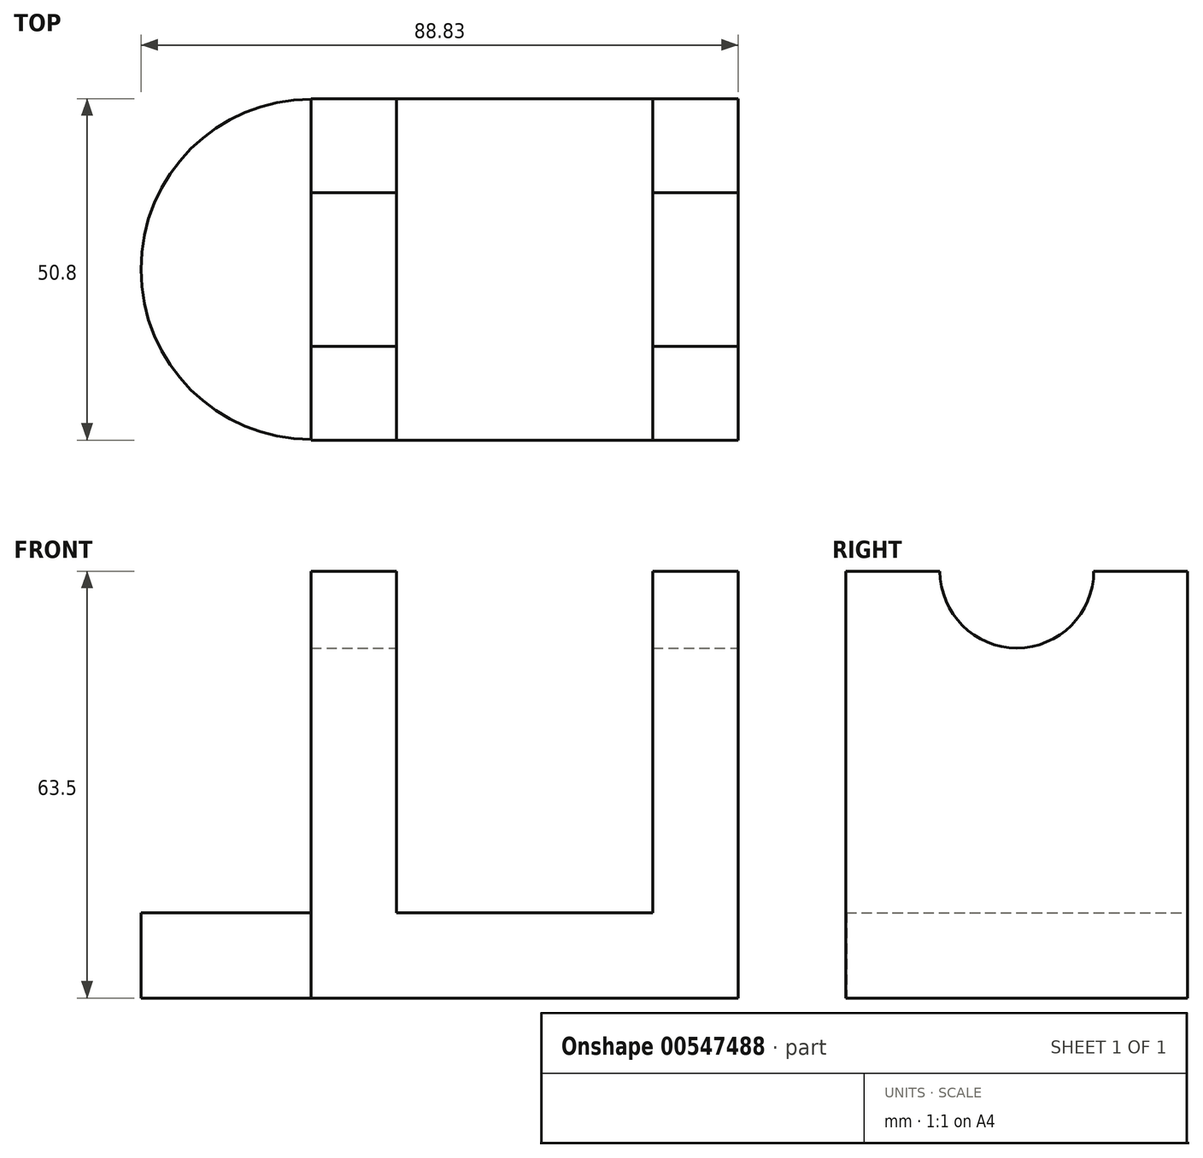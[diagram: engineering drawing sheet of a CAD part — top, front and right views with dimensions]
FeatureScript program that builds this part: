
annotation { "Feature Type Name" : "Feature", "Feature Type Description" : "" }
export const myFeature = defineFeature(function(context is Context, id is Id, definition is map)
    precondition{}
    {
        {
            var Q0;
            Q0=qCreatedBy(makeId("Front.planeOp"),FACE);
            var sketch = newSketch(context, id + "F0", { "sketchPlane" : qUnion([Q0])});
            skLineSegment(sketch, "E0", {"start": v(0, 0) * mm, "end": v(-31.75, 0) * mm});
            skLineSegment(sketch, "E1", {"start": v(-31.75, 0) * mm, "end": v(-31.75, 63.5) * mm});
            skLineSegment(sketch, "E2.MirrorCS", {"start": v(31.75, 0) * mm, "end": v(31.75, 63.5) * mm});
            skLineSegment(sketch, "E3.MirrorCS", {"start": v(0, 0) * mm, "end": v(31.75, 0) * mm});
            skLineSegment(sketch, "E4.0", {"start": v(-19.05, 12.7) * mm, "end": v(-19.05, 63.5) * mm});
            skLineSegment(sketch, "E4.1", {"start": v(0, 12.7) * mm, "end": v(-19.05, 12.7) * mm});
            skLineSegment(sketch, "E4.2", {"start": v(0, 12.7) * mm, "end": v(19.05, 12.7) * mm});
            skLineSegment(sketch, "E4.3", {"start": v(19.05, 12.7) * mm, "end": v(19.05, 63.5) * mm});
            skLineSegment(sketch, "E5", {"start": v(-31.75, 63.5) * mm, "end": v(-19.05, 63.5) * mm});
            skLineSegment(sketch, "E6", {"start": v(19.05, 63.5) * mm, "end": v(31.75, 63.5) * mm});
            skSolve(sketch);
        }
        {
            var Q0;
            Q0=makeQuery(id+"F0.imprint","IMPRINT",FACE,{"disambiguationData":[TD([[makeQuery(id+"F0.imprint","IMPRINT",EDGE,{"derivedFrom":sQuery(id+"F0.wireOp",EDGE,"E0")}),-1.0]])]});
            extrude(context, id + "F1", {"entities" : qUnion([Q0]), "endBound" : BoundingType.SYMMETRIC, "depth" : 50.8 * mm, "offsetDistance" : 25.4 * mm});
        }
        {
            var Q0;
            Q0=makeQuery(id+"F1.opExtrude","SWEPT_FACE",FACE,{"disambiguationData":[OSD([sQuery(id+"F0.wireOp",EDGE,"E2.MirrorCS")])]});
            var sketch = newSketch(context, id + "F2", { "sketchPlane" : qUnion([Q0])});
            skCircle(sketch, "E7", {"center": v(0, 63.5) * mm, "radius": 11.43 * mm});
            skSolve(sketch);
        }
        {
            var Q0;
            {var subQ0=sQuery(id+"F2.wireOp",EDGE,"E7");var subQ1=makeQuery(id+"F1.opExtrude","SWEPT_EDGE",EDGE,{"disambiguationData":[OSD([sQuery(id+"F0.wireOp",EDGE,"E2.MirrorCS"),sQuery(id+"F0.wireOp",EDGE,"E6")])]});var subQ2=makeQuery(id+"F2.imprint","INTERSECT",VERTEX,{"disambiguationData":[OD(0.0)],"derivedFrom":[subQ1,subQ0]});Q0=makeQuery(id+"F2.imprint","IMPRINT",FACE,{"disambiguationData":[TD([[makeQuery(id+"F2.imprint","IMPRINT",EDGE,{"disambiguationData":[TD([[subQ2,1.0]])],"derivedFrom":subQ0}),1.0]])]});}
            extrude(context, id + "F3", {"entities" : qUnion([Q0]), "operationType" : NewBodyOperationType.REMOVE, "endBound" : BoundingType.THROUGH_ALL, "oppositeDirection" : true, "depth" : 25.4 * mm, "offsetDistance" : 25.4 * mm});
        }
        {
            var Q0;
            Q0=makeQuery(id+"F1.opExtrude","SWEPT_FACE",FACE,{"disambiguationData":[OSD([sQuery(id+"F0.wireOp",EDGE,"E0"),sQuery(id+"F0.wireOp",EDGE,"E3.MirrorCS")])]});
            var sketch = newSketch(context, id + "F4", { "sketchPlane" : qUnion([Q0])});
            skCircle(sketch, "E8", {"center": v(-31.75, 0) * mm, "radius": 25.33 * mm});
            skCircle(sketch, "E9.MirrorC", {"center": v(31.75, 0) * mm, "radius": 25.33 * mm});
            skSolve(sketch);
        }
        {
            var Q0;
            {var subQ0=sQuery(id+"F4.wireOp",EDGE,"E8");var subQ1=makeQuery(id+"F1.opExtrude","SWEPT_EDGE",EDGE,{"disambiguationData":[OSD([sQuery(id+"F0.wireOp",EDGE,"E0"),sQuery(id+"F0.wireOp",EDGE,"E1")])]});var subQ2=makeQuery(id+"F4.imprint","INTERSECT",VERTEX,{"disambiguationData":[OD(0.0)],"derivedFrom":[subQ1,subQ0]});Q0=makeQuery(id+"F4.imprint","IMPRINT",FACE,{"disambiguationData":[TD([[makeQuery(id+"F4.imprint","IMPRINT",EDGE,{"disambiguationData":[TD([[subQ2,1.0]])],"derivedFrom":subQ0}),1.0]])]});}
            var Q1;
            {var subQ0=sQuery(id+"F4.wireOp",EDGE,"E9.MirrorC");var subQ1=makeQuery(id+"F1.opExtrude","SWEPT_EDGE",EDGE,{"disambiguationData":[OSD([sQuery(id+"F0.wireOp",EDGE,"E2.MirrorCS"),sQuery(id+"F0.wireOp",EDGE,"E3.MirrorCS")])]});var subQ2=makeQuery(id+"F4.imprint","INTERSECT",VERTEX,{"disambiguationData":[OD(0.0)],"derivedFrom":[subQ1,subQ0]});Q1=makeQuery(id+"F4.imprint","IMPRINT",FACE,{"disambiguationData":[TD([[makeQuery(id+"F4.imprint","IMPRINT",EDGE,{"disambiguationData":[TD([[subQ2,1.0]])],"derivedFrom":subQ0}),-1.0]])]});}
            extrude(context, id + "F5", {"entities" : qUnion([Q0, Q1]), "operationType" : NewBodyOperationType.ADD, "oppositeDirection" : true, "depth" : 12.7 * mm, "offsetDistance" : 25.4 * mm});
        }
    });
